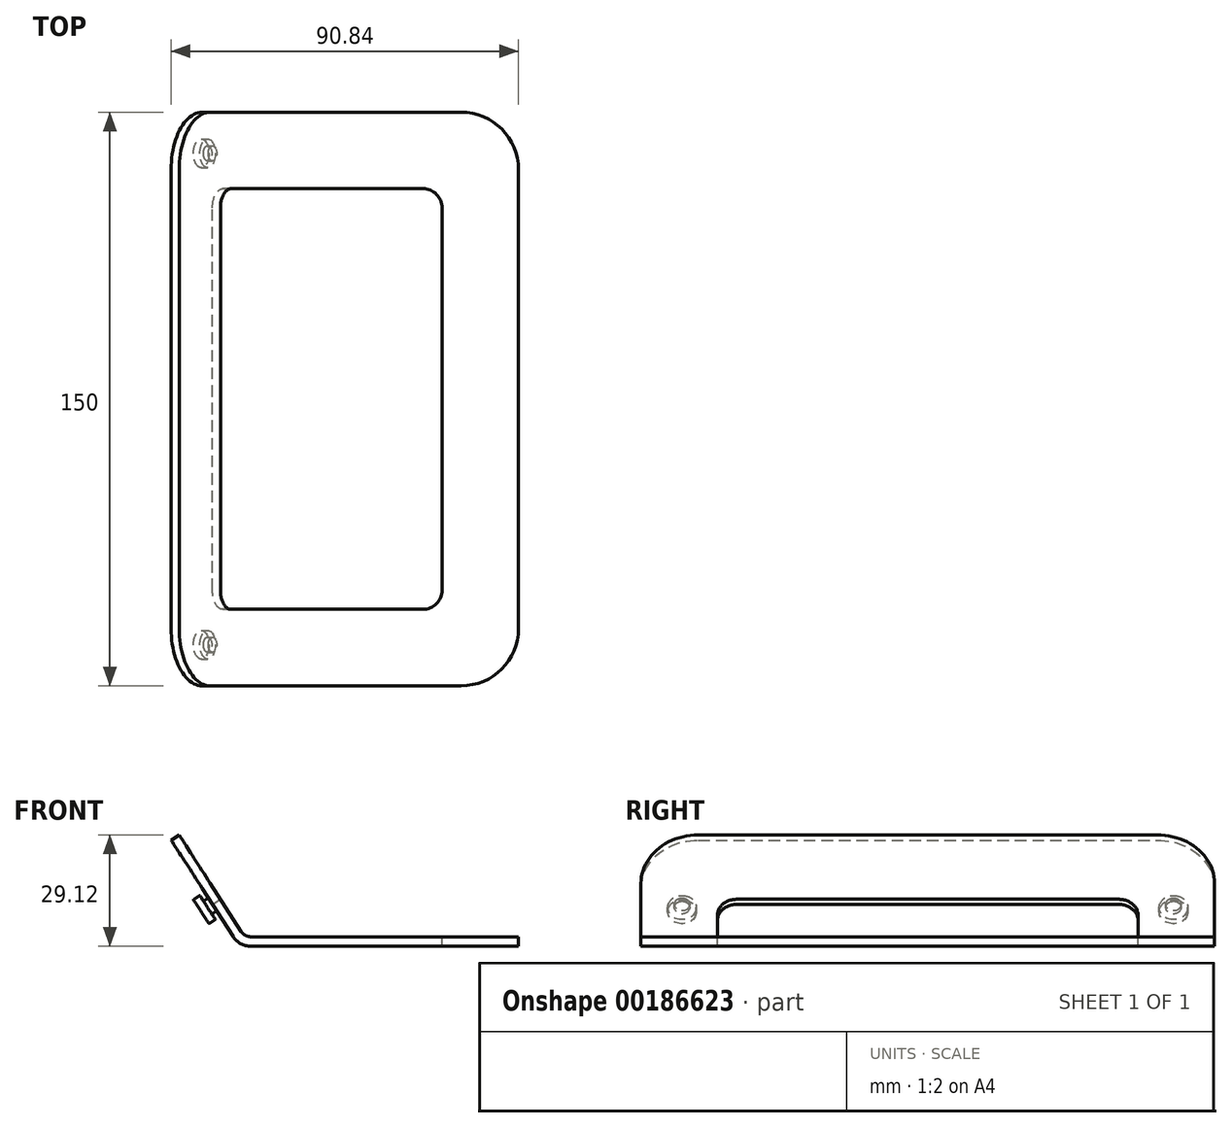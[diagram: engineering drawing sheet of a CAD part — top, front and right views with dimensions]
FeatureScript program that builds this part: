
annotation { "Feature Type Name" : "Feature", "Feature Type Description" : "" }
export const myFeature = defineFeature(function(context is Context, id is Id, definition is map)
    precondition{}
    {
        {
            var Q0;
            Q0=qCreatedBy(makeId("Front.planeOp"),FACE);
            var sketch = newSketch(context, id + "F0", { "sketchPlane" : qUnion([Q0])});
            skLineSegment(sketch, "E0.bottom", {"start": v(35, 1.25) * mm, "end": v(-35, 1.25) * mm});
            skLineSegment(sketch, "E0.top", {"start": v(35, -1.25) * mm, "end": v(-35, -1.25) * mm});
            skLineSegment(sketch, "E0.left", {"start": v(35, 1.25) * mm, "end": v(35, -1.25) * mm});
            skLineSegment(sketch, "E0.right", {"start": v(-35, 1.25) * mm, "end": v(-35, -1.25) * mm});
            skPoint(sketch, "E0.middle", {"position": v(0, 0) * mm});
            skArc(sketch, "E1", {"start": v(-39.63, 1.28) * mm, "mid": v(-37.64, -0.58) * mm, "end": v(-35, -1.25) * mm});
            skArc(sketch, "E2", {"start": v(-37.52, 2.63) * mm, "mid": v(-36.44, 1.62) * mm, "end": v(-35, 1.25) * mm});
            skLineSegment(sketch, "E3", {"start": v(-39.63, 1.28) * mm, "end": v(-37.52, 2.63) * mm});
            skLineSegment(sketch, "E4", {"start": v(-39.63, 1.28) * mm, "end": v(-55.84, 26.52) * mm});
            skLineSegment(sketch, "E5", {"start": v(-55.84, 26.52) * mm, "end": v(-53.73, 27.87) * mm});
            skLineSegment(sketch, "E6", {"start": v(-53.73, 27.87) * mm, "end": v(-37.52, 2.63) * mm});
            skSolve(sketch);
        }
        {
            var Q0;
            Q0 = qSketchRegion(id + "F0", true);
            extrude(context, id + "F1", {"entities" : qUnion([Q0]), "depth" : 150 * mm});
        }
        {
            var Q0;
            Q0=makeQuery(id+"F1.opExtrude","SWEPT_FACE",FACE,{"disambiguationData":[OSD([sQuery(id+"F0.wireOp",EDGE,"E0.bottom")])]});
            var sketch = newSketch(context, id + "F2", { "sketchPlane" : qUnion([Q0])});
            skLineSegment(sketch, "E7.bottom", {"start": v(15, -20) * mm, "end": v(-37.52, -20) * mm});
            skLineSegment(sketch, "E7.top", {"start": v(15, -130) * mm, "end": v(-37.52, -130) * mm});
            skLineSegment(sketch, "E7.left", {"start": v(15, -20) * mm, "end": v(15, -130) * mm});
            skLineSegment(sketch, "E7.right", {"start": v(-37.52, -20) * mm, "end": v(-37.52, -130) * mm});
            skSolve(sketch);
        }
        {
            var Q0;
            Q0 = qSketchRegion(id + "F2", true);
            extrude(context, id + "F3", {"entities" : qUnion([Q0]), "operationType" : NewBodyOperationType.REMOVE, "endBound" : BoundingType.THROUGH_ALL, "oppositeDirection" : true, "depth" : 25 * mm});
        }
        {
            var Q0;
            Q0=makeQuery(id+"F1.opExtrude","SWEPT_FACE",FACE,{"disambiguationData":[OSD([sQuery(id+"F0.wireOp",EDGE,"E6")])]});
            var sketch = newSketch(context, id + "F4", { "sketchPlane" : qUnion([Q0])});
            skLineSegment(sketch, "E8.bottom", {"start": v(-20, 32.49) * mm, "end": v(-130, 32.49) * mm});
            skLineSegment(sketch, "E8.top", {"start": v(-20, 2.49) * mm, "end": v(-130, 2.49) * mm});
            skLineSegment(sketch, "E8.left", {"start": v(-20, 32.49) * mm, "end": v(-20, 2.49) * mm});
            skLineSegment(sketch, "E8.right", {"start": v(-130, 32.49) * mm, "end": v(-130, 2.49) * mm});
            skSolve(sketch);
        }
        {
            var Q0;
            Q0 = qSketchRegion(id + "F4", true);
            extrude(context, id + "F5", {"entities" : qUnion([Q0]), "operationType" : NewBodyOperationType.REMOVE, "endBound" : BoundingType.THROUGH_ALL, "oppositeDirection" : true, "depth" : 25 * mm});
        }
        {
            var Q0;
            Q0 = qSketchRegion(id + "F4", true);
            extrude(context, id + "F6", {"entities" : qUnion([Q0]), "operationType" : NewBodyOperationType.REMOVE, "endBound" : BoundingType.THROUGH_ALL, "depth" : 25 * mm});
        }
        {
            var Q0;
            Q0=makeQuery(id+"F1.opExtrude","SWEPT_FACE",FACE,{"disambiguationData":[OSD([sQuery(id+"F0.wireOp",EDGE,"E4")])]});
            var sketch = newSketch(context, id + "F7", { "sketchPlane" : qUnion([Q0])});
            skCircle(sketch, "E9", {"center": v(139.25, 32.49) * mm, "radius": 2 * mm});
            skCircle(sketch, "E10", {"center": v(10.75, 32.49) * mm, "radius": 2 * mm});
            skSolve(sketch);
        }
        {
            var Q0;
            Q0=makeQuery(id+"F7.imprint","IMPRINT",FACE,{"disambiguationData":[TD([[makeQuery(id+"F7.imprint","IMPRINT",EDGE,{"derivedFrom":sQuery(id+"F7.wireOp",EDGE,"E10")}),1.0]])]});
            var Q1;
            Q1=makeQuery(id+"F7.imprint","IMPRINT",FACE,{"disambiguationData":[TD([[makeQuery(id+"F7.imprint","IMPRINT",EDGE,{"derivedFrom":sQuery(id+"F7.wireOp",EDGE,"E9")}),1.0]])]});
            extrude(context, id + "F8", {"entities" : qUnion([Q0, Q1]), "operationType" : NewBodyOperationType.ADD, "depth" : 1.5 * mm});
        }
        {
            var Q0;
            Q0=makeQuery(id+"F8.opExtrude","CAP_FACE",FACE,{"disambiguationData":[OSD([sQuery(id+"F7.wireOp",EDGE,"E10")])],"isStart":false});
            var sketch = newSketch(context, id + "F9", { "sketchPlane" : qUnion([Q0])});
            skCircle(sketch, "E11", {"center": v(10.75, 32.49) * mm, "radius": 3.75 * mm});
            skSolve(sketch);
        }
        {
            var Q0;
            Q0=makeQuery(id+"F8.opExtrude","CAP_FACE",FACE,{"disambiguationData":[OSD([sQuery(id+"F7.wireOp",EDGE,"E9")])],"isStart":false});
            var sketch = newSketch(context, id + "F10", { "sketchPlane" : qUnion([Q0])});
            skCircle(sketch, "E12", {"center": v(139.25, 32.49) * mm, "radius": 3.75 * mm});
            skSolve(sketch);
        }
        {
            var Q0;
            Q0 = qSketchRegion(id + "F9", true);
            var Q1;
            Q1 = qSketchRegion(id + "F10", true);
            extrude(context, id + "F11", {"entities" : qUnion([Q0, Q1]), "operationType" : NewBodyOperationType.ADD, "depth" : 2 * mm});
        }
        {
            var Q0;
            Q0=makeQuery(id+"F1.opExtrude","CAP_EDGE",EDGE,{"disambiguationData":[OSD([sQuery(id+"F0.wireOp",EDGE,"E5")])],"isStart":true});
            fillet(context, id + "F12", {"entities" : qUnion([Q0]), "radius" : 15 * mm, "tangentPropagation" : true, "allowEdgeOverflow" : false});
        }
        {
            var Q0;
            Q0=makeQuery(id+"F1.opExtrude","CAP_EDGE",EDGE,{"disambiguationData":[OSD([sQuery(id+"F0.wireOp",EDGE,"E5")])],"isStart":false});
            var Q1;
            Q1=makeQuery(id+"F1.opExtrude","CAP_EDGE",EDGE,{"disambiguationData":[OSD([sQuery(id+"F0.wireOp",EDGE,"E0.left")])],"isStart":false});
            var Q2;
            Q2=makeQuery(id+"F1.opExtrude","CAP_EDGE",EDGE,{"disambiguationData":[OSD([sQuery(id+"F0.wireOp",EDGE,"E0.left")])],"isStart":true});
            fillet(context, id + "F13", {"entities" : qUnion([Q0, Q1, Q2]), "radius" : 15 * mm, "tangentPropagation" : true, "allowEdgeOverflow" : false});
        }
        {
            var Q0;
            Q0=makeQuery(id+"F5.boolean.opBoolean","COPY",EDGE,{"derivedFrom":makeQuery(id+"F5.opExtrude","SWEPT_EDGE",EDGE,{"disambiguationData":[OSD([sQuery(id+"F4.wireOp",EDGE,"E8.bottom"),sQuery(id+"F4.wireOp",EDGE,"E8.left")])]})});
            var Q1;
            Q1=makeQuery(id+"F3.boolean.opBoolean","COPY",EDGE,{"derivedFrom":makeQuery(id+"F3.opExtrude","SWEPT_EDGE",EDGE,{"disambiguationData":[OSD([sQuery(id+"F2.wireOp",EDGE,"E7.bottom"),sQuery(id+"F2.wireOp",EDGE,"E7.left")])]})});
            var Q2;
            Q2=makeQuery(id+"F3.boolean.opBoolean","COPY",EDGE,{"derivedFrom":makeQuery(id+"F3.opExtrude","SWEPT_EDGE",EDGE,{"disambiguationData":[OSD([sQuery(id+"F2.wireOp",EDGE,"E7.top"),sQuery(id+"F2.wireOp",EDGE,"E7.left")])]})});
            var Q3;
            Q3=makeQuery(id+"F5.boolean.opBoolean","COPY",EDGE,{"derivedFrom":makeQuery(id+"F5.opExtrude","SWEPT_EDGE",EDGE,{"disambiguationData":[OSD([sQuery(id+"F4.wireOp",EDGE,"E8.bottom"),sQuery(id+"F4.wireOp",EDGE,"E8.right")])]})});
            fillet(context, id + "F14", {"entities" : qUnion([Q0, Q1, Q2, Q3]), "radius" : 5 * mm, "tangentPropagation" : true, "allowEdgeOverflow" : false});
        }
    });
